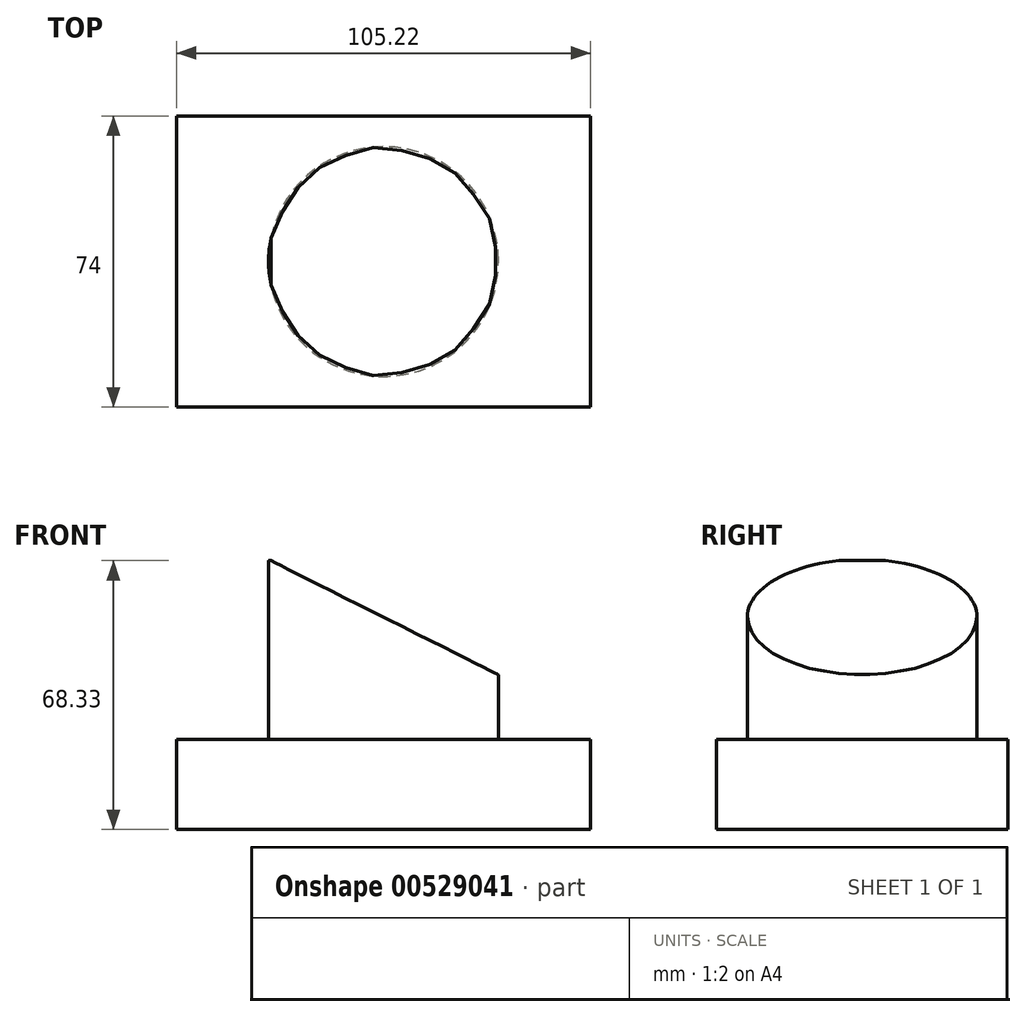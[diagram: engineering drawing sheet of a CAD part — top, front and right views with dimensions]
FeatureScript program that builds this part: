
annotation { "Feature Type Name" : "Feature", "Feature Type Description" : "" }
export const myFeature = defineFeature(function(context is Context, id is Id, definition is map)
    precondition{}
    {
        {
            var Q0;
            Q0=qCreatedBy(makeId("Top.planeOp"),FACE);
            var sketch = newSketch(context, id + "F0", { "sketchPlane" : qUnion([Q0])});
            skLineSegment(sketch, "E0.bottom", {"start": v(-52.6, 37) * mm, "end": v(52.6, 37) * mm});
            skLineSegment(sketch, "E0.top", {"start": v(-52.6, -37) * mm, "end": v(52.6, -37) * mm});
            skLineSegment(sketch, "E0.left", {"start": v(-52.6, 37) * mm, "end": v(-52.6, -37) * mm});
            skLineSegment(sketch, "E0.right", {"start": v(52.6, 37) * mm, "end": v(52.6, -37) * mm});
            skPoint(sketch, "E0.middle", {"position": v(0, 0) * mm});
            skCircle(sketch, "E1", {"center": v(0, 0) * mm, "radius": 22.39 * mm});
            skSolve(sketch);
        }
        {
            var Q0;
            Q0 = qSketchRegion(id + "F0", true);
            var Q1;
            Q1=makeQuery(id+"F0.imprint","IMPRINT",FACE,{"disambiguationData":[TD([[makeQuery(id+"F0.imprint","IMPRINT",EDGE,{"derivedFrom":sQuery(id+"F0.wireOp",EDGE,"E1")}),1.0]])]});
            extrude(context, id + "F1", {"entities" : qUnion([Q0, Q1]), "depth" : 22.86 * mm, "offsetDistance" : 25.4 * mm});
        }
        {
            var Q0;
            Q0=makeQuery(id+"F0.imprint","IMPRINT",FACE,{"disambiguationData":[TD([[makeQuery(id+"F0.imprint","IMPRINT",EDGE,{"derivedFrom":sQuery(id+"F0.wireOp",EDGE,"E1")}),1.0]])]});
            extrude(context, id + "F2", {"entities" : qUnion([Q0]), "operationType" : NewBodyOperationType.ADD, "depth" : 59.94 * mm, "offsetDistance" : 25.4 * mm});
        }
        {
            var Q0;
            Q0=makeQuery(id+"F2.opExtrude","CAP_FACE",FACE,{"disambiguationData":[OSD([sQuery(id+"F0.wireOp",EDGE,"E1")])],"isStart":false});
            extrude(context, id + "F3", {"entities" : qUnion([Q0]), "operationType" : NewBodyOperationType.REMOVE, "oppositeDirection" : true, "depth" : 25.4 * mm, "offsetDistance" : 25.4 * mm});
        }
        {
            var Q0;
            Q0=makeQuery(id+"F3.boolean.opBoolean","COPY",FACE,{"derivedFrom":makeQuery(id+"F3.opExtrude","CAP_FACE",FACE,{"disambiguationData":[OSD([sQuery(id+"F0.wireOp",EDGE,"E1")])],"isStart":false})});
            extrude(context, id + "F4", {"entities" : qUnion([Q0]), "operationType" : NewBodyOperationType.ADD, "depth" : 25.4 * mm, "offsetDistance" : 25.4 * mm, "hasDraft" : true, "draftAngle" : 3 * degree});
        }
        {
            var Q0;
            Q0=makeQuery(id+"F4.opExtrude","CAP_FACE",FACE,{"disambiguationData":[OSD([sQuery(id+"F0.wireOp",EDGE,"E1")])],"isStart":false});
            extrude(context, id + "F5", {"entities" : qUnion([Q0]), "operationType" : NewBodyOperationType.REMOVE, "oppositeDirection" : true, "depth" : 25.4 * mm, "offsetDistance" : 25.4 * mm, "hasSecondDirection" : true, "secondDirectionOppositeDirection" : false, "secondDirectionDepth" : 25.4 * mm});
        }
        {
            var Q0;
            Q0=makeQuery(id+"F5.boolean.opBoolean","COPY",FACE,{"derivedFrom":makeQuery(id+"F5.opExtrude","CAP_FACE",FACE,{"disambiguationData":[OSD([sQuery(id+"F0.wireOp",EDGE,"E1")])],"isStart":false})});
            extrude(context, id + "F6", {"entities" : qUnion([Q0]), "operationType" : NewBodyOperationType.REMOVE, "oppositeDirection" : true, "depth" : 25.4 * mm, "offsetDistance" : 25.4 * mm, "hasDraft" : true, "draftAngle" : 15 * degree});
        }
        {
            var Q0;
            Q0=makeQuery(id+"F6.boolean.opBoolean","COPY",FACE,{"derivedFrom":makeQuery(id+"F6.opExtrude","CAP_FACE",FACE,{"disambiguationData":[OSD([sQuery(id+"F0.wireOp",EDGE,"E1")])],"isStart":false})});
            extrude(context, id + "F7", {"entities" : qUnion([Q0]), "operationType" : NewBodyOperationType.ADD, "depth" : 59.18 * mm, "offsetDistance" : 25.4 * mm});
        }
        {
            var Q0;
            Q0=qCreatedBy(makeId("Front.planeOp"),FACE);
            var sketch = newSketch(context, id + "F8", { "sketchPlane" : qUnion([Q0])});
            skLineSegment(sketch, "E2", {"start": v(-29.52, 68.8) * mm, "end": v(38.5, 34.65) * mm});
            skLineSegment(sketch, "E3", {"start": v(38.5, 34.65) * mm, "end": v(50.83, 89.59) * mm});
            skLineSegment(sketch, "E4", {"start": v(50.83, 89.59) * mm, "end": v(-21.82, 85.74) * mm});
            skLineSegment(sketch, "E5", {"start": v(-21.82, 85.74) * mm, "end": v(-29.52, 68.8) * mm});
            skSolve(sketch);
        }
        {
            var Q0;
            Q0=makeQuery(id+"F8.imprint","IMPRINT",FACE,{"disambiguationData":[TD([[makeQuery(id+"F8.imprint","IMPRINT",EDGE,{"derivedFrom":sQuery(id+"F8.wireOp",EDGE,"E2")}),1.0]])]});
            extrude(context, id + "F9", {"entities" : qUnion([Q0]), "operationType" : NewBodyOperationType.REMOVE, "endBound" : BoundingType.SYMMETRIC, "oppositeDirection" : true, "depth" : 66.55 * mm, "offsetDistance" : 25.4 * mm});
        }
    });
